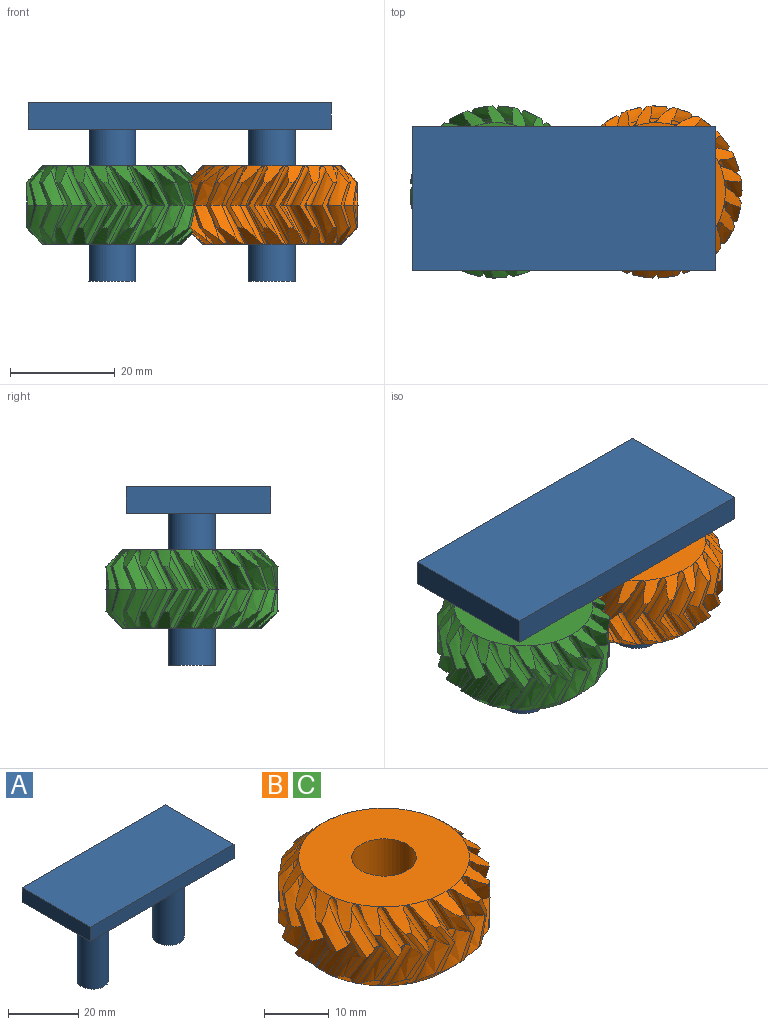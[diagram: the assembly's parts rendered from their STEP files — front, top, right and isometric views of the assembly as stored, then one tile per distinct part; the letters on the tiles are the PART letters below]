
ASSEMBLY  parts=3 mates=3
PART A: 10 faces, bbox 57.9x27.6x34 mm
  f0: cylinder r=4.5mm len=29mm, axis (0,0,1), area 820mm2, adj f1,f8
  f1: plane 9x9mm, normal (0,0,-1), area 63.6mm2, adj f0
  f2: cylinder r=4.5mm len=29mm, axis (0,0,1), area 820mm2, adj f3,f8
  f3: plane 9x9mm, normal (0,0,-1), area 63.6mm2, adj f2
  f4: plane 57.87x5mm, normal (0,1,0), area 289.3mm2, adj f5,f7,f8,f9
  f5: plane 27.58x5mm, normal (-1,0,0), area 137.9mm2, adj f4,f6,f8,f9
  f6: plane 57.87x5mm, normal (0,-1,0), area 289.3mm2, adj f5,f7,f8,f9
  f7: plane 27.58x5mm, normal (1,0,0), area 137.9mm2, adj f4,f6,f8,f9
  f8: plane 57.87x27.58mm, normal (0,0,-1), area 1468.6mm2, adj f0,f2,f4,f5,f6,f7
  f9: plane 57.87x27.58mm, normal (0,0,1), area 1595.9mm2, adj f4,f5,f6,f7
PART B: 234 faces, bbox 33.3x33.4x17.7 mm
  f0: cylinder r=16.43mm len=8.61mm, axis (0,0,-1), area 8.6mm2, adj f98,f103,f184,f187,f192,f213
  f1: cylinder r=16.43mm len=8.61mm, axis (0,0,-1), area 8.6mm2, adj f78,f99,f164,f183,f193,f214
  f2: cylinder r=16.43mm len=8.61mm, axis (0,0,-1), area 8.6mm2, adj f90,f95,f176,f179,f195,f216
  f3: cylinder r=16.43mm len=8.61mm, axis (0,0,-1), area 8.6mm2, adj f91,f102,f175,f188,f191,f212
  f4: cylinder r=16.43mm len=8.61mm, axis (0,0,-1), area 8.6mm2, adj f82,f87,f168,f171,f197,f218
  f5: cylinder r=16.43mm len=8.61mm, axis (0,0,-1), area 8.6mm2, adj f30,f83,f116,f167,f198,f219
  f6: cylinder r=16.43mm len=8.61mm, axis (0,0,-1), area 8.6mm2, adj f74,f79,f160,f163,f199,f220
  f7: cylinder r=16.43mm len=8.61mm, axis (0,0,-1), area 8.6mm2, adj f75,f86,f159,f172,f196,f217
  f8: cylinder r=16.43mm len=8.61mm, axis (0,0,-1), area 8.6mm2, adj f46,f67,f132,f151,f202,f223
  f9: cylinder r=16.43mm len=8.61mm, axis (0,0,-1), area 8.6mm2, adj f58,f63,f144,f147,f204,f225
  f10: cylinder r=16.43mm len=8.61mm, axis (0,0,-1), area 8.6mm2, adj f59,f70,f143,f156,f200,f221
  f11: cylinder r=16.43mm len=8.61mm, axis (0,0,-1), area 8.6mm2, adj f50,f55,f136,f139,f206,f227
  f12: cylinder r=16.43mm len=8.61mm, axis (0,0,-1), area 8.6mm2, adj f51,f94,f135,f180,f194,f215
  f13: cylinder r=16.43mm len=8.61mm, axis (0,0,-1), area 8.6mm2, adj f42,f47,f128,f131,f207,f228
  f14: cylinder r=16.43mm len=8.61mm, axis (0,0,-1), area 8.6mm2, adj f43,f54,f127,f140,f205,f226
  f15: cylinder r=16.43mm len=8.61mm, axis (0,0,-1), area 8.6mm2, adj f34,f39,f120,f123,f209,f230
  f16: cylinder r=16.43mm len=8.61mm, axis (0,0,-1), area 8.6mm2, adj f21,f35,f107,f119,f210,f231
  f17: cylinder r=16.43mm len=8.61mm, axis (0,0,-1), area 8.6mm2, adj f26,f31,f112,f115,f211,f232
  f18: cylinder r=16.43mm len=8.61mm, axis (0,0,-1), area 8.6mm2, adj f27,f38,f111,f124,f208,f229
  f19: cylinder r=16.43mm len=8.61mm, axis (0,0,-1), area 8.6mm2, adj f22,f62,f106,f148,f203,f224
  f20: cylinder r=16.43mm len=8.61mm, axis (0,0,-1), area 8.6mm2, adj f66,f71,f152,f155,f201,f222
  f21: bspline ~9.07x6.16mm, area 15.8mm2, adj f16,f24,f107,f210
  f22: bspline ~9.07x6.53mm, area 15.8mm2, adj f19,f23,f106,f203
  f23: bspline ~9.45x5.47mm, area 9.5mm2, adj f22,f24,f25,f108,f203
  f24: bspline ~10.19x5.69mm, area 9.5mm2, adj f21,f23,f25,f109,f210
  f25: plane 26.47x26.47mm, normal (0,0,1), area 471.5mm2, adj f23,f24,f28,f29,f32,f33,f36,f37
  f26: bspline ~9.07x6.27mm, area 15.8mm2, adj f17,f29,f112,f211
  f27: bspline ~9.07x6.26mm, area 15.8mm2, adj f18,f28,f111,f208
  f28: bspline ~9.45x4.24mm, area 9.5mm2, adj f25,f27,f29,f113,f208
  f29: bspline ~10.19x4.65mm, area 9.5mm2, adj f25,f26,f28,f114,f211
  f30: bspline ~9.07x5.32mm, area 15.8mm2, adj f5,f33,f116,f198
  f31: bspline ~9.07x6.75mm, area 15.8mm2, adj f17,f32,f115,f211
  f32: bspline ~9.45x5.07mm, area 9.5mm2, adj f25,f31,f33,f117,f211
  f33: bspline ~10.19x4.99mm, area 9.5mm2, adj f25,f30,f32,f118,f198
  f34: bspline ~9.07x6.64mm, area 15.8mm2, adj f15,f37,f120,f209
  f35: bspline ~9.07x6.01mm, area 15.8mm2, adj f16,f36,f119,f210
  f36: bspline ~9.45x5.25mm, area 9.5mm2, adj f25,f35,f37,f121,f210
  f37: bspline ~10.19x5.85mm, area 9.5mm2, adj f25,f34,f36,f122,f209
  f38: bspline ~9.07x6.76mm, area 15.8mm2, adj f18,f41,f124,f208
  f39: bspline ~9.07x5.33mm, area 15.8mm2, adj f15,f40,f123,f209
  f40: bspline ~9.45x4.76mm, area 9.5mm2, adj f25,f39,f41,f125,f209
  f41: bspline ~10.19x5.49mm, area 9.5mm2, adj f25,f38,f40,f126,f208
  f42: bspline ~9.07x5.65mm, area 15.8mm2, adj f13,f45,f128,f207
  f43: bspline ~9.07x6.77mm, area 15.8mm2, adj f14,f44,f127,f205
  f44: bspline ~9.45x5.32mm, area 9.5mm2, adj f25,f43,f45,f129,f205
  f45: bspline ~10.19x5.33mm, area 9.5mm2, adj f25,f42,f44,f130,f207
  f46: bspline ~9.07x6.31mm, area 15.8mm2, adj f8,f49,f132,f202
  f47: bspline ~9.07x6.43mm, area 15.8mm2, adj f13,f48,f131,f207
  f48: bspline ~9.45x5.46mm, area 9.5mm2, adj f25,f47,f49,f133,f207
  f49: bspline ~10.19x5.78mm, area 9.5mm2, adj f25,f46,f48,f134,f202
  f50: bspline ~9.07x6.59mm, area 15.8mm2, adj f11,f53,f136,f206
  f51: bspline ~9.07x5.81mm, area 15.8mm2, adj f12,f52,f135,f194
  f52: bspline ~9.45x4.41mm, area 9.5mm2, adj f25,f51,f53,f137,f194
  f53: bspline ~10.19x5.13mm, area 9.5mm2, adj f25,f50,f52,f138,f206
  f54: bspline ~9.07x5.82mm, area 15.8mm2, adj f14,f57,f140,f205
  f55: bspline ~9.07x6.58mm, area 15.8mm2, adj f11,f56,f139,f206
  f56: bspline ~9.45x4.71mm, area 9.5mm2, adj f25,f55,f57,f141,f206
  f57: bspline ~10.19x4.65mm, area 9.5mm2, adj f25,f54,f56,f142,f205
  f58: bspline ~9.07x6.06mm, area 15.8mm2, adj f9,f61,f144,f204
  f59: bspline ~9.07x6.44mm, area 15.8mm2, adj f10,f60,f143,f200
  f60: bspline ~9.45x4.49mm, area 9.5mm2, adj f25,f59,f61,f145,f200
  f61: bspline ~10.19x4.47mm, area 9.5mm2, adj f25,f58,f60,f146,f204
  f62: bspline ~9.07x5.48mm, area 15.8mm2, adj f19,f65,f148,f203
  f63: bspline ~9.07x6.78mm, area 15.8mm2, adj f9,f64,f147,f204
  f64: bspline ~9.45x5.21mm, area 9.5mm2, adj f25,f63,f65,f149,f204
  f65: bspline ~10.19x5.17mm, area 9.5mm2, adj f25,f62,f64,f150,f203
  f66: bspline ~9.07x6.72mm, area 15.8mm2, adj f20,f69,f152,f201
  f67: bspline ~9.07x5.84mm, area 15.8mm2, adj f8,f68,f151,f202
  f68: bspline ~9.45x5.14mm, area 9.5mm2, adj f25,f67,f69,f153,f202
  f69: bspline ~10.19x5.81mm, area 9.5mm2, adj f25,f66,f68,f154,f201
  f70: bspline ~9.07x6.69mm, area 15.8mm2, adj f10,f73,f156,f200
  f71: bspline ~9.07x5.53mm, area 15.8mm2, adj f20,f72,f155,f201
  f72: bspline ~9.45x4.58mm, area 9.5mm2, adj f25,f71,f73,f157,f201
  f73: bspline ~10.19x5.33mm, area 9.5mm2, adj f25,f70,f72,f158,f200
  f74: bspline ~9.07x6.78mm, area 15.8mm2, adj f6,f77,f160,f199
  f75: bspline ~9.07x5.49mm, area 15.8mm2, adj f7,f76,f159,f196
  f76: bspline ~9.45x4.91mm, area 9.5mm2, adj f25,f75,f77,f161,f196
  f77: bspline ~10.19x5.63mm, area 9.5mm2, adj f25,f74,f76,f162,f199
  f78: bspline ~9.07x6.45mm, area 15.8mm2, adj f1,f81,f164,f193
  f79: bspline ~9.07x6.05mm, area 15.8mm2, adj f6,f80,f163,f199
  f80: bspline ~9.45x4.26mm, area 9.5mm2, adj f25,f79,f81,f165,f199
  f81: bspline ~10.19x4.9mm, area 9.5mm2, adj f25,f78,f80,f166,f193
  f82: bspline ~9.07x6mm, area 15.8mm2, adj f4,f85,f168,f197
  f83: bspline ~9.07x6.64mm, area 15.8mm2, adj f5,f84,f167,f198
  f84: bspline ~9.45x5.45mm, area 9.5mm2, adj f25,f83,f85,f169,f198
  f85: bspline ~10.19x5.57mm, area 9.5mm2, adj f25,f82,f84,f170,f197
  f86: bspline ~9.07x6.52mm, area 15.8mm2, adj f7,f89,f172,f196
  f87: bspline ~9.07x6.17mm, area 15.8mm2, adj f4,f88,f171,f197
  f88: bspline ~9.45x5.35mm, area 9.5mm2, adj f25,f87,f89,f173,f197
  f89: bspline ~10.19x5.86mm, area 9.5mm2, adj f25,f86,f88,f174,f196
  f90: bspline ~9.07x6.43mm, area 15.8mm2, adj f2,f93,f176,f195
  f91: bspline ~9.07x6.31mm, area 15.8mm2, adj f3,f92,f175,f191
  f92: bspline ~9.45x5.42mm, area 9.5mm2, adj f25,f91,f93,f177,f191
  f93: bspline ~10.19x5.83mm, area 9.5mm2, adj f25,f90,f92,f178,f195
  f94: bspline ~9.07x6.77mm, area 15.8mm2, adj f12,f97,f180,f194
  f95: bspline ~9.07x5.66mm, area 15.8mm2, adj f2,f96,f179,f195
  f96: bspline ~9.45x5.04mm, area 9.5mm2, adj f25,f95,f97,f181,f195
  f97: bspline ~10.19x5.74mm, area 9.5mm2, adj f25,f94,f96,f182,f194
  f98: bspline ~9.07x5.54mm, area 15.8mm2, adj f0,f101,f184,f192
  f99: bspline ~9.07x6.69mm, area 15.8mm2, adj f1,f100,f183,f193
  f100: bspline ~9.45x4.9mm, area 9.5mm2, adj f25,f99,f101,f185,f193
  f101: bspline ~10.19x4.81mm, area 9.5mm2, adj f25,f98,f100,f186,f192
  f102: bspline ~9.07x5.83mm, area 15.8mm2, adj f3,f105,f188,f191
  f103: bspline ~9.07x6.73mm, area 15.8mm2, adj f0,f104,f187,f192
  f104: bspline ~9.45x5.4mm, area 9.5mm2, adj f25,f103,f105,f189,f192
  f105: bspline ~10.19x5.45mm, area 9.5mm2, adj f25,f102,f104,f190,f191
  f106: bspline ~9.07x6.62mm, area 15.8mm2, adj f19,f22,f108,f224
  f107: bspline ~9.07x6.03mm, area 15.8mm2, adj f16,f21,f109,f231
  f108: bspline ~10.19x5.85mm, area 9.5mm2, adj f23,f106,f109,f110,f224
  f109: bspline ~9.45x5.27mm, area 9.5mm2, adj f24,f107,f108,f110,f231
  f110: plane 26.47x26.47mm, normal (0,0,-1), area 471.5mm2, adj f108,f109,f113,f114,f117,f118,f121,f122
  f111: bspline ~9.07x6.09mm, area 15.8mm2, adj f18,f27,f113,f229
  f112: bspline ~9.07x6.42mm, area 15.8mm2, adj f17,f26,f114,f232
  f113: bspline ~10.19x4.44mm, area 9.5mm2, adj f28,f110,f111,f114,f229
  f114: bspline ~9.45x4.45mm, area 9.5mm2, adj f29,f110,f112,f113,f232
  f115: bspline ~9.07x6.7mm, area 15.8mm2, adj f17,f31,f117,f232
  f116: bspline ~9.07x5.48mm, area 15.8mm2, adj f5,f30,f118,f219
  f117: bspline ~10.19x5.35mm, area 9.5mm2, adj f32,f110,f115,f118,f232
  f118: bspline ~9.45x4.6mm, area 9.5mm2, adj f33,f110,f116,f117,f219
  f119: bspline ~9.07x6.14mm, area 15.8mm2, adj f16,f35,f121,f231
  f120: bspline ~9.07x6.54mm, area 15.8mm2, adj f15,f34,f122,f230
  f121: bspline ~10.19x5.67mm, area 9.5mm2, adj f36,f110,f119,f122,f231
  f122: bspline ~9.45x5.47mm, area 9.5mm2, adj f37,f110,f120,f121,f230
  f123: bspline ~9.07x5.46mm, area 15.8mm2, adj f15,f39,f125,f230
  f124: bspline ~9.07x6.78mm, area 15.8mm2, adj f18,f38,f126,f229
  f125: bspline ~10.19x5.15mm, area 9.5mm2, adj f40,f110,f123,f126,f230
  f126: bspline ~9.45x5.19mm, area 9.5mm2, adj f41,f110,f124,f125,f229
  f127: bspline ~9.07x6.78mm, area 15.8mm2, adj f14,f43,f129,f226
  f128: bspline ~9.07x5.52mm, area 15.8mm2, adj f13,f42,f130,f228
  f129: bspline ~10.19x5.65mm, area 9.5mm2, adj f44,f110,f127,f130,f226
  f130: bspline ~9.45x4.93mm, area 9.5mm2, adj f45,f110,f128,f129,f228
  f131: bspline ~9.07x6.51mm, area 15.8mm2, adj f13,f47,f133,f228
  f132: bspline ~9.07x6.19mm, area 15.8mm2, adj f8,f46,f134,f223
  f133: bspline ~10.19x5.86mm, area 9.5mm2, adj f48,f110,f131,f134,f228
  f134: bspline ~9.45x5.36mm, area 9.5mm2, adj f49,f110,f132,f133,f223
  f135: bspline ~9.07x5.58mm, area 15.8mm2, adj f12,f51,f137,f215
  f136: bspline ~9.07x6.67mm, area 15.8mm2, adj f11,f50,f138,f227
  f137: bspline ~10.19x4.79mm, area 9.5mm2, adj f52,f110,f135,f138,f215
  f138: bspline ~9.45x4.88mm, area 9.5mm2, adj f53,f110,f136,f137,f227
  f139: bspline ~9.07x6.47mm, area 15.8mm2, adj f11,f55,f141,f227
  f140: bspline ~9.07x6.02mm, area 15.8mm2, adj f14,f54,f142,f226
  f141: bspline ~10.19x4.94mm, area 9.5mm2, adj f56,f110,f139,f142,f227
  f142: bspline ~9.45x4.29mm, area 9.5mm2, adj f57,f110,f140,f141,f226
  f143: bspline ~9.07x6.3mm, area 15.8mm2, adj f10,f59,f145,f221
  f144: bspline ~9.07x6.24mm, area 15.8mm2, adj f9,f58,f146,f225
  f145: bspline ~10.19x4.69mm, area 9.5mm2, adj f60,f110,f143,f146,f221
  f146: bspline ~9.45x4.2mm, area 9.5mm2, adj f61,f110,f144,f145,f225
  f147: bspline ~9.07x6.76mm, area 15.8mm2, adj f9,f63,f149,f225
  f148: bspline ~9.07x5.35mm, area 15.8mm2, adj f19,f62,f150,f224
  f149: bspline ~10.19x5.52mm, area 9.5mm2, adj f64,f110,f147,f150,f225
  f150: bspline ~9.45x4.78mm, area 9.5mm2, adj f65,f110,f148,f149,f224
  f151: bspline ~9.07x5.97mm, area 15.8mm2, adj f8,f67,f153,f223
  f152: bspline ~9.07x6.66mm, area 15.8mm2, adj f20,f66,f154,f222
  f153: bspline ~10.19x5.55mm, area 9.5mm2, adj f68,f110,f151,f154,f223
  f154: bspline ~9.45x5.45mm, area 9.5mm2, adj f69,f110,f152,f153,f222
  f155: bspline ~9.07x5.3mm, area 15.8mm2, adj f20,f71,f157,f222
  f156: bspline ~9.07x6.75mm, area 15.8mm2, adj f10,f70,f158,f221
  f157: bspline ~10.19x4.96mm, area 9.5mm2, adj f72,f110,f155,f158,f222
  f158: bspline ~9.45x5.05mm, area 9.5mm2, adj f73,f110,f156,f157,f221
  f159: bspline ~9.07x5.63mm, area 15.8mm2, adj f7,f75,f161,f217
  f160: bspline ~9.07x6.78mm, area 15.8mm2, adj f6,f74,f162,f220
  f161: bspline ~10.19x5.31mm, area 9.5mm2, adj f76,f110,f159,f162,f217
  f162: bspline ~9.45x5.31mm, area 9.5mm2, adj f77,f110,f160,f161,f220
  f163: bspline ~9.07x5.86mm, area 15.8mm2, adj f6,f79,f165,f220
  f164: bspline ~9.07x6.56mm, area 15.8mm2, adj f1,f78,f166,f214
  f165: bspline ~10.19x4.63mm, area 9.5mm2, adj f80,f110,f163,f166,f220
  f166: bspline ~9.45x4.68mm, area 9.5mm2, adj f81,f110,f164,f165,f214
  f167: bspline ~9.07x6.71mm, area 15.8mm2, adj f5,f83,f169,f219
  f168: bspline ~9.07x5.86mm, area 15.8mm2, adj f4,f82,f170,f218
  f169: bspline ~10.19x5.82mm, area 9.5mm2, adj f84,f110,f167,f170,f219
  f170: bspline ~9.45x5.15mm, area 9.5mm2, adj f85,f110,f168,f169,f218
  f171: bspline ~9.07x6.29mm, area 15.8mm2, adj f4,f87,f173,f218
  f172: bspline ~9.07x6.45mm, area 15.8mm2, adj f7,f86,f174,f217
  f173: bspline ~10.19x5.77mm, area 9.5mm2, adj f88,f110,f171,f174,f218
  f174: bspline ~9.45x5.47mm, area 9.5mm2, adj f89,f110,f172,f173,f217
  f175: bspline ~9.07x6.41mm, area 15.8mm2, adj f3,f91,f177,f212
  f176: bspline ~9.07x6.33mm, area 15.8mm2, adj f2,f90,f178,f216
  f177: bspline ~10.19x5.83mm, area 9.5mm2, adj f92,f110,f175,f178,f212
  f178: bspline ~9.45x5.43mm, area 9.5mm2, adj f93,f110,f176,f177,f216
  f179: bspline ~9.07x5.8mm, area 15.8mm2, adj f2,f95,f181,f216
  f180: bspline ~9.07x6.74mm, area 15.8mm2, adj f12,f94,f182,f215
  f181: bspline ~10.19x5.44mm, area 9.5mm2, adj f96,f110,f179,f182,f216
  f182: bspline ~9.45x5.39mm, area 9.5mm2, adj f97,f110,f180,f181,f215
  f183: bspline ~9.07x6.61mm, area 15.8mm2, adj f1,f99,f185,f214
  f184: bspline ~9.07x5.77mm, area 15.8mm2, adj f0,f98,f186,f213
  f185: bspline ~10.19x5.16mm, area 9.5mm2, adj f100,f110,f183,f186,f214
  f186: bspline ~9.45x4.43mm, area 9.5mm2, adj f101,f110,f184,f185,f213
  f187: bspline ~9.07x6.77mm, area 15.8mm2, adj f0,f103,f189,f213
  f188: bspline ~9.07x5.69mm, area 15.8mm2, adj f3,f102,f190,f212
  f189: bspline ~10.19x5.75mm, area 9.5mm2, adj f104,f110,f187,f190,f213
  f190: bspline ~9.45x5.06mm, area 9.5mm2, adj f105,f110,f188,f189,f212
  f191: cone r=13.23mm half-angle=45deg, axis (0,0,-1), area 9.5mm2, adj f3,f25,f91,f92,f102,f105
  f192: cone r=13.23mm half-angle=45deg, axis (0,0,-1), area 9.5mm2, adj f0,f25,f98,f101,f103,f104
  f193: cone r=13.23mm half-angle=45deg, axis (0,0,-1), area 9.5mm2, adj f1,f25,f78,f81,f99,f100
  f194: cone r=13.23mm half-angle=45deg, axis (0,0,-1), area 9.5mm2, adj f12,f25,f51,f52,f94,f97
  f195: cone r=13.23mm half-angle=45deg, axis (0,0,-1), area 9.5mm2, adj f2,f25,f90,f93,f95,f96
  f196: cone r=13.23mm half-angle=45deg, axis (0,0,-1), area 9.5mm2, adj f7,f25,f75,f76,f86,f89
  f197: cone r=13.23mm half-angle=45deg, axis (0,0,-1), area 9.5mm2, adj f4,f25,f82,f85,f87,f88
  f198: cone r=13.23mm half-angle=45deg, axis (0,0,-1), area 9.5mm2, adj f5,f25,f30,f33,f83,f84
  f199: cone r=13.23mm half-angle=45deg, axis (0,0,-1), area 9.5mm2, adj f6,f25,f74,f77,f79,f80
  f200: cone r=13.23mm half-angle=45deg, axis (0,0,-1), area 9.5mm2, adj f10,f25,f59,f60,f70,f73
  f201: cone r=13.23mm half-angle=45deg, axis (0,0,-1), area 9.5mm2, adj f20,f25,f66,f69,f71,f72
  f202: cone r=13.23mm half-angle=45deg, axis (0,0,-1), area 9.5mm2, adj f8,f25,f46,f49,f67,f68
  f203: cone r=13.23mm half-angle=45deg, axis (0,0,-1), area 9.5mm2, adj f19,f22,f23,f25,f62,f65
  f204: cone r=13.23mm half-angle=45deg, axis (0,0,-1), area 9.5mm2, adj f9,f25,f58,f61,f63,f64
  f205: cone r=13.23mm half-angle=45deg, axis (0,0,-1), area 9.5mm2, adj f14,f25,f43,f44,f54,f57
  f206: cone r=13.23mm half-angle=45deg, axis (0,0,-1), area 9.5mm2, adj f11,f25,f50,f53,f55,f56
  f207: cone r=13.23mm half-angle=45deg, axis (0,0,-1), area 9.5mm2, adj f13,f25,f42,f45,f47,f48
  f208: cone r=13.23mm half-angle=45deg, axis (0,0,-1), area 9.5mm2, adj f18,f25,f27,f28,f38,f41
  f209: cone r=13.23mm half-angle=45deg, axis (0,0,-1), area 9.5mm2, adj f15,f25,f34,f37,f39,f40
  f210: cone r=13.23mm half-angle=45deg, axis (0,0,-1), area 9.5mm2, adj f16,f21,f24,f25,f35,f36
  f211: cone r=13.23mm half-angle=45deg, axis (0,0,-1), area 9.5mm2, adj f17,f25,f26,f29,f31,f32
  f212: cone r=13.23mm half-angle=45deg, axis (0,0,1), area 9.5mm2, adj f3,f110,f175,f177,f188,f190
  f213: cone r=13.23mm half-angle=45deg, axis (0,0,1), area 9.5mm2, adj f0,f110,f184,f186,f187,f189
  f214: cone r=13.23mm half-angle=45deg, axis (0,0,1), area 9.5mm2, adj f1,f110,f164,f166,f183,f185
  f215: cone r=13.23mm half-angle=45deg, axis (0,0,1), area 9.5mm2, adj f12,f110,f135,f137,f180,f182
  f216: cone r=13.23mm half-angle=45deg, axis (0,0,1), area 9.5mm2, adj f2,f110,f176,f178,f179,f181
  f217: cone r=13.23mm half-angle=45deg, axis (0,0,1), area 9.5mm2, adj f7,f110,f159,f161,f172,f174
  f218: cone r=13.23mm half-angle=45deg, axis (0,0,1), area 9.5mm2, adj f4,f110,f168,f170,f171,f173
  f219: cone r=13.23mm half-angle=45deg, axis (0,0,1), area 9.5mm2, adj f5,f110,f116,f118,f167,f169
  f220: cone r=13.23mm half-angle=45deg, axis (0,0,1), area 9.5mm2, adj f6,f110,f160,f162,f163,f165
  f221: cone r=13.23mm half-angle=45deg, axis (0,0,1), area 9.5mm2, adj f10,f110,f143,f145,f156,f158
  f222: cone r=13.23mm half-angle=45deg, axis (0,0,1), area 9.5mm2, adj f20,f110,f152,f154,f155,f157
  f223: cone r=13.23mm half-angle=45deg, axis (0,0,1), area 9.5mm2, adj f8,f110,f132,f134,f151,f153
  f224: cone r=13.23mm half-angle=45deg, axis (0,0,1), area 9.5mm2, adj f19,f106,f108,f110,f148,f150
  f225: cone r=13.23mm half-angle=45deg, axis (0,0,1), area 9.5mm2, adj f9,f110,f144,f146,f147,f149
  f226: cone r=13.23mm half-angle=45deg, axis (0,0,1), area 9.5mm2, adj f14,f110,f127,f129,f140,f142
  f227: cone r=13.23mm half-angle=45deg, axis (0,0,1), area 9.5mm2, adj f11,f110,f136,f138,f139,f141
  f228: cone r=13.23mm half-angle=45deg, axis (0,0,1), area 9.5mm2, adj f13,f110,f128,f130,f131,f133
  f229: cone r=13.23mm half-angle=45deg, axis (0,0,1), area 9.5mm2, adj f18,f110,f111,f113,f124,f126
  f230: cone r=13.23mm half-angle=45deg, axis (0,0,1), area 9.5mm2, adj f15,f110,f120,f122,f123,f125
  f231: cone r=13.23mm half-angle=45deg, axis (0,0,1), area 9.5mm2, adj f16,f107,f109,f110,f119,f121
  f232: cone r=13.23mm half-angle=45deg, axis (0,0,1), area 9.5mm2, adj f17,f110,f112,f114,f115,f117
  f233: cylinder r=5mm len=15mm, axis (0,0,-1), area 471.2mm2, adj f25,f110
PART C: same geometry as B
PLACE A t=(-3.98,2.92,-5.97)mm fixed
PLACE B rot(axis=(0.94,0.35,0),180deg) t=(26.52,2.92,-0.47)mm
PLACE C rot(axis=(0,0,-1),41.4deg) t=(-3.98,2.92,-0.47)mm
MATE revolute A.f0 <-> C.f233  axis (0,0,1) through (-3.98,2.92,-0.47)mm
MATE planar C.f110 <-> B.f25  axis (0,0,-1) through (2.89,-8.38,-7.97)mm
MATE cylindrical B.f233 <-> A.f2  axis (0,0,-1) through (26.52,2.92,-7.97)mm
